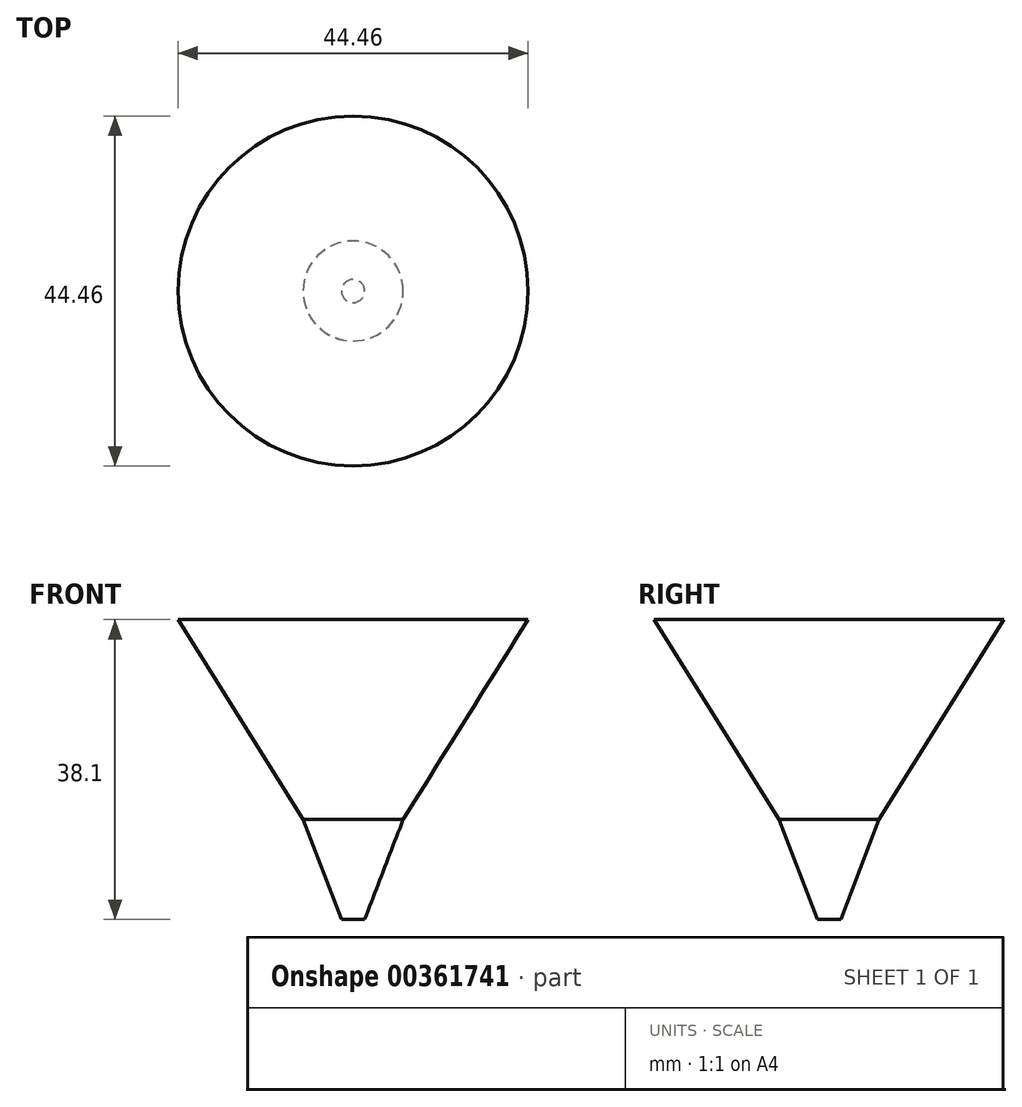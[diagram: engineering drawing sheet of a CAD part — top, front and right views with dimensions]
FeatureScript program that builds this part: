
annotation { "Feature Type Name" : "Feature", "Feature Type Description" : "" }
export const myFeature = defineFeature(function(context is Context, id is Id, definition is map)
    precondition{}
    {
        {
            var Q0;
            Q0=qCreatedBy(makeId("Top.planeOp"),FACE);
            var sketch = newSketch(context, id + "F0", { "sketchPlane" : qUnion([Q0])});
            skCircle(sketch, "E0", {"center": v(0, 0) * mm, "radius": 22.23 * mm});
            skSolve(sketch);
        }
        {
            var Q0;
            Q0 = qSketchRegion(id + "F0", true);
            extrude(context, id + "F1", {"entities" : qUnion([Q0]), "oppositeDirection" : true, "depth" : 25.4 * mm, "hasDraft" : true, "draftAngle" : 32 * degree, "draftPullDirection" : true});
        }
        {
            var Q0;
            Q0=qCreatedBy(makeId("Top.planeOp"),FACE);
            cPlane(context, id + "F2", {"entities" : qUnion([Q0]), "cplaneType" : CPlaneType.OFFSET, "offset" : 25.4 * mm, "oppositeDirection" : true, "width" : 152.4 * mm, "height" : 152.4 * mm});
        }
        {
            var Q0;
            Q0=qCreatedBy(id+"F2.planeOp",FACE);
            var sketch = newSketch(context, id + "F3", { "sketchPlane" : qUnion([Q0])});
            skCircle(sketch, "E1", {"center": v(0, 0) * mm, "radius": 6.35 * mm});
            skSolve(sketch);
        }
        {
            var Q0;
            Q0 = qSketchRegion(id + "F3", true);
            extrude(context, id + "F4", {"entities" : qUnion([Q0]), "oppositeDirection" : true, "depth" : 12.7 * mm, "hasDraft" : true, "draftAngle" : 21 * degree, "draftPullDirection" : true});
        }
    });
